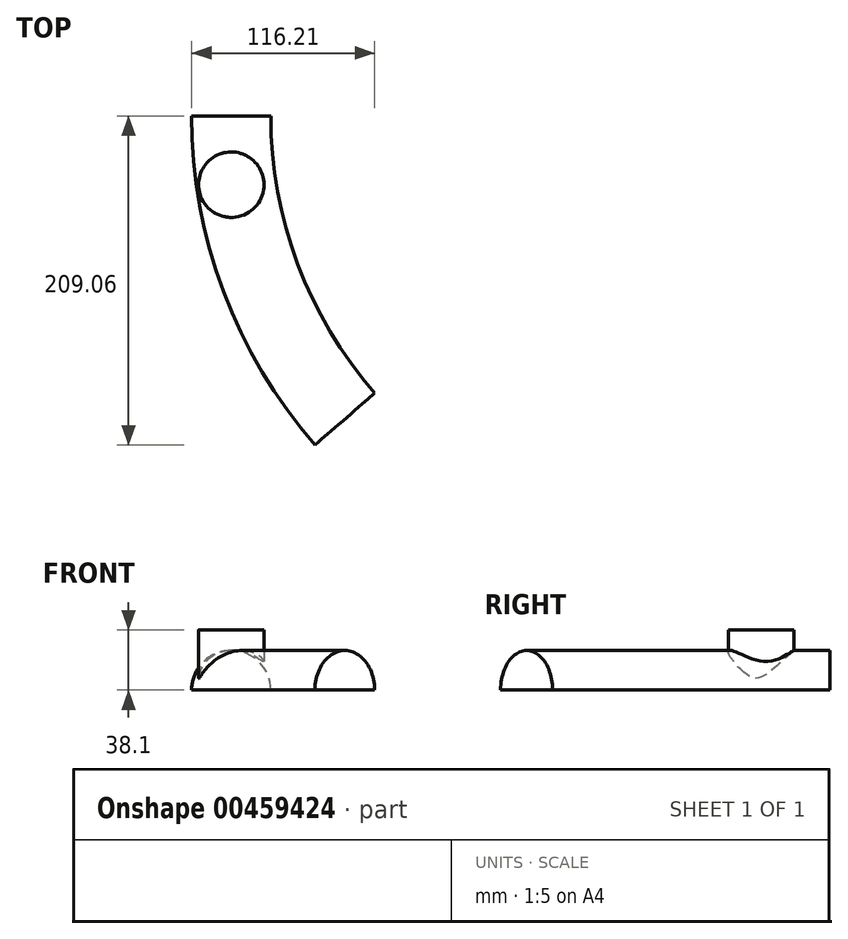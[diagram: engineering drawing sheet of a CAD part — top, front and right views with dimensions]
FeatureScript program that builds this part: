
annotation { "Feature Type Name" : "Feature", "Feature Type Description" : "" }
export const myFeature = defineFeature(function(context is Context, id is Id, definition is map)
    precondition{}
    {
        {
            var Q0;
            Q0=qCreatedBy(makeId("Top.planeOp"),FACE);
            var sketch = newSketch(context, id + "F0", { "sketchPlane" : qUnion([Q0])});
            skLineSegment(sketch, "E0", {"start": v(0, 0) * mm, "end": v(0, -43.68) * mm});
            skCircle(sketch, "E1", {"center": v(0, -43.68) * mm, "radius": 20.77 * mm});
            skSolve(sketch);
        }
        {
            var Q0;
            {var subQ0=sQuery(id+"F0.wireOp",EDGE,"E1");Q0=makeQuery(id+"F0.imprint","IMPRINT",FACE,{"disambiguationData":[TD([[makeQuery(id+"F0.imprint","IMPRINT",EDGE,{"derivedFrom":subQ0}),1.0]])]});}
            extrude(context, id + "F1", {"entities" : qUnion([Q0]), "depth" : 38.1 * mm});
        }
        {
            var Q0;
            Q0=qCreatedBy(makeId("Top.planeOp"),FACE);
            var sketch = newSketch(context, id + "F2", { "sketchPlane" : qUnion([Q0])});
            skArc(sketch, "E2", {"start": v(-72.14, -192.55) * mm, "mid": v(-18.63, -102.8) * mm, "end": v(0, 0) * mm});
            skLineSegment(sketch, "E3", {"start": v(0, 0) * mm, "end": v(0, -167.15) * mm, "construction": true});
            skArc(sketch, "E4.MirrorCS", {"start": v(72.14, -192.55) * mm, "mid": v(18.63, -102.8) * mm, "end": v(0, 0) * mm});
            skSolve(sketch);
        }
        {
            var Q0;
            Q0=qCreatedBy(makeId("Front.planeOp"),FACE);
            var sketch = newSketch(context, id + "F3", { "sketchPlane" : qUnion([Q0])});
            skLineSegment(sketch, "E5", {"start": v(25.13, 0) * mm, "end": v(-25.13, 0) * mm});
            skArc(sketch, "E6", {"start": v(25.13, 0) * mm, "mid": v(0, 25.13) * mm, "end": v(-25.13, 0) * mm});
            skSolve(sketch);
        }
        {
            var Q0;
            Q0=makeQuery(id+"F3.imprint","IMPRINT",FACE,{"disambiguationData":[TD([[makeQuery(id+"F3.imprint","IMPRINT",EDGE,{"derivedFrom":sQuery(id+"F3.wireOp",EDGE,"E5")}),-1.0]])]});
            var Q1;
            Q1=sQuery(id+"F2.wireOp",EDGE,"E4.MirrorCS");
            sweep(context, id + "F4", {"operationType" : NewBodyOperationType.ADD, "profiles" : qUnion([Q0]), "path" : qUnion([Q1])});
        }
    });
